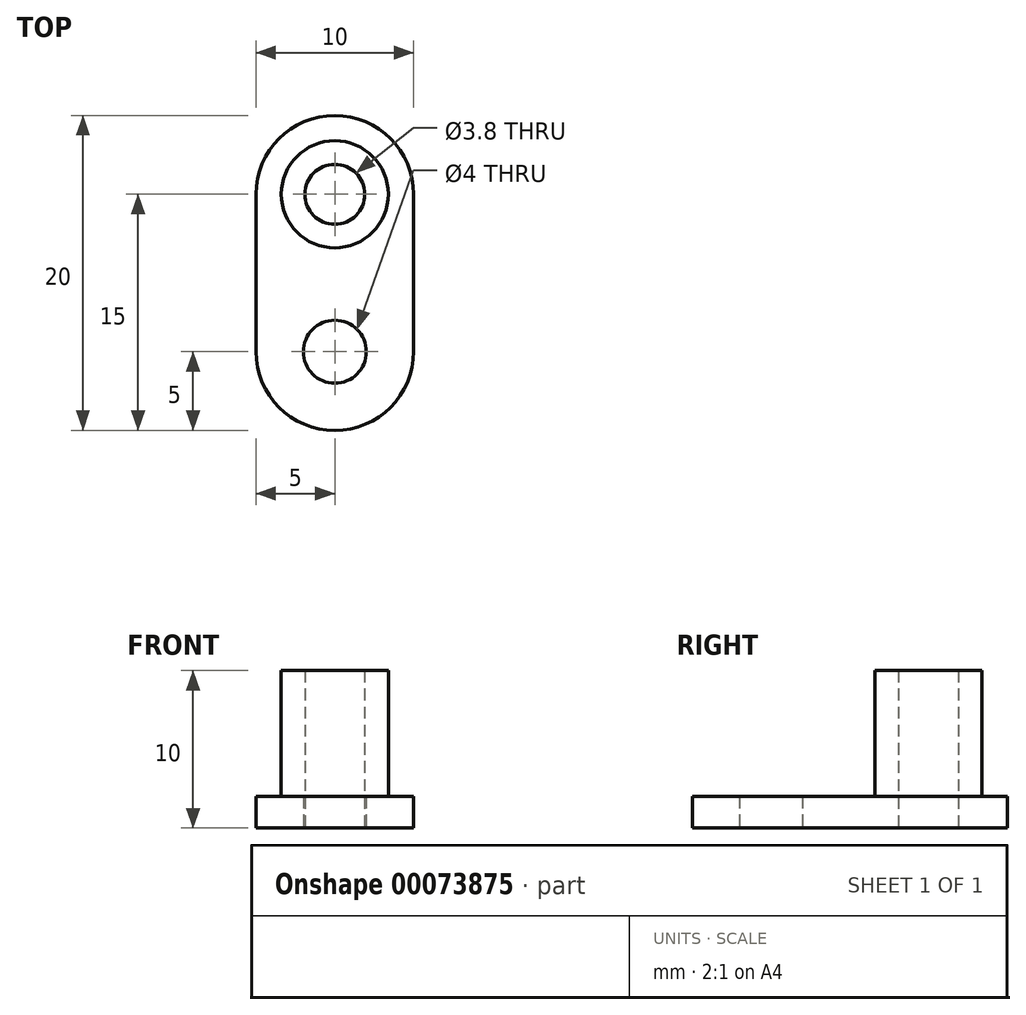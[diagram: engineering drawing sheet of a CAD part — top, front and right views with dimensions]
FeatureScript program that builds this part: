
annotation { "Feature Type Name" : "Feature", "Feature Type Description" : "" }
export const myFeature = defineFeature(function(context is Context, id is Id, definition is map)
    precondition{}
    {
        {
            var Q0;
            Q0=qCreatedBy(makeId("Top.planeOp"),FACE);
            var sketch = newSketch(context, id + "F0", { "sketchPlane" : qUnion([Q0])});
            skCircle(sketch, "E0", {"center": v(0, -6) * mm, "radius": 5 * mm});
            skCircle(sketch, "E1", {"center": v(0, 4) * mm, "radius": 5 * mm});
            skLineSegment(sketch, "E2", {"start": v(-5, 4) * mm, "end": v(-5, -6) * mm});
            skLineSegment(sketch, "E3", {"start": v(5, 4) * mm, "end": v(5, -6) * mm});
            skCircle(sketch, "E4", {"center": v(0, 4) * mm, "radius": 1.9 * mm});
            skCircle(sketch, "E5", {"center": v(0, 4) * mm, "radius": 3.4 * mm});
            skCircle(sketch, "E6", {"center": v(0, -6) * mm, "radius": 2 * mm});
            skSolve(sketch);
        }
        {
            var Q0;
            Q0=makeQuery(id+"F0.imprint","IMPRINT",FACE,{"disambiguationData":[TD([[makeQuery(id+"F0.imprint","IMPRINT",EDGE,{"derivedFrom":sQuery(id+"F0.wireOp",EDGE,"E4")}),-1.0]])]});
            extrude(context, id + "F1", {"entities" : qUnion([Q0]), "depth" : 10 * mm});
        }
        {
            var Q0;
            Q0=makeQuery(id+"F0.imprint","IMPRINT",FACE,{"disambiguationData":[TD([[makeQuery(id+"F0.imprint","IMPRINT",EDGE,{"derivedFrom":sQuery(id+"F0.wireOp",EDGE,"E5")}),-1.0]])]});
            var Q1;
            {var subQ0=sQuery(id+"F0.wireOp",EDGE,"E3");Q1=makeQuery(id+"F0.imprint","IMPRINT",FACE,{"disambiguationData":[TD([[makeQuery(id+"F0.imprint","IMPRINT",EDGE,{"derivedFrom":subQ0}),-1.0]])]});}
            var Q2;
            Q2=makeQuery(id+"F0.imprint","IMPRINT",FACE,{"disambiguationData":[TD([[makeQuery(id+"F0.imprint","IMPRINT",EDGE,{"derivedFrom":sQuery(id+"F0.wireOp",EDGE,"E6")}),-1.0]])]});
            var Q3;
            {var subQ0=sQuery(id+"F0.wireOp",EDGE,"E2");Q3=makeQuery(id+"F0.imprint","IMPRINT",FACE,{"disambiguationData":[TD([[makeQuery(id+"F0.imprint","IMPRINT",EDGE,{"derivedFrom":subQ0}),1.0]])]});}
            extrude(context, id + "F2", {"entities" : qUnion([Q0, Q1, Q2, Q3]), "operationType" : NewBodyOperationType.ADD, "depth" : 2 * mm});
        }
    });
